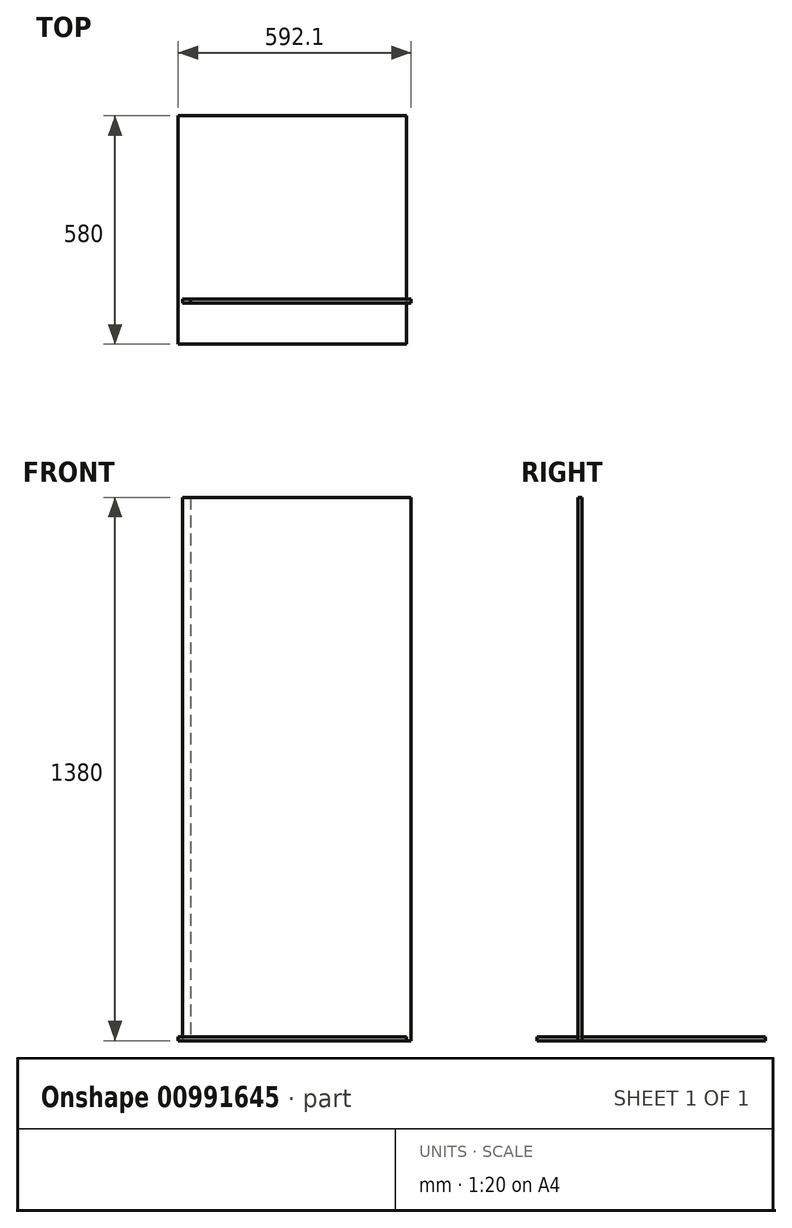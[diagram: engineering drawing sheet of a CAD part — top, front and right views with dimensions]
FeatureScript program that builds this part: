
annotation { "Feature Type Name" : "Feature", "Feature Type Description" : "" }
export const myFeature = defineFeature(function(context is Context, id is Id, definition is map)
    precondition{}
    {
        {
            var Q0;
            Q0=qCreatedBy(makeId("Top.planeOp"),FACE);
            var sketch = newSketch(context, id + "F0", { "sketchPlane" : qUnion([Q0])});
            skLineSegment(sketch, "E0.bottom", {"start": v(-278.4, -47.98) * mm, "end": v(301.6, -47.98) * mm});
            skLineSegment(sketch, "E0.top", {"start": v(-278.4, -57.98) * mm, "end": v(301.6, -57.98) * mm});
            skLineSegment(sketch, "E0.left", {"start": v(-278.4, -47.98) * mm, "end": v(-278.4, -57.98) * mm});
            skLineSegment(sketch, "E0.right", {"start": v(301.6, -47.98) * mm, "end": v(301.6, -57.98) * mm});
            skSolve(sketch);
        }
        {
            var Q0;
            Q0=qCreatedBy(makeId("Top.planeOp"),FACE);
            var sketch = newSketch(context, id + "F1", { "sketchPlane" : qUnion([Q0])});
            skLineSegment(sketch, "E1.bottom", {"start": v(-257.6, -47.91) * mm, "end": v(302.4, -47.91) * mm});
            skLineSegment(sketch, "E1.top", {"start": v(-257.6, -57.91) * mm, "end": v(302.4, -57.91) * mm});
            skLineSegment(sketch, "E1.left", {"start": v(-257.6, -47.91) * mm, "end": v(-257.6, -57.91) * mm});
            skLineSegment(sketch, "E1.right", {"start": v(302.4, -47.91) * mm, "end": v(302.4, -57.91) * mm});
            skSolve(sketch);
        }
        {
            var Q0;
            Q0 = qSketchRegion(id + "F0", true);
            extrude(context, id + "F2", {"entities" : qUnion([Q0]), "depth" : 1380 * mm, "offsetDistance" : 25 * mm});
        }
        {
            var Q0;
            Q0 = qSketchRegion(id + "F1", true);
            extrude(context, id + "F3", {"entities" : qUnion([Q0]), "depth" : 1380 * mm, "offsetDistance" : 25 * mm});
        }
        {
            var Q0;
            Q0=qCreatedBy(makeId("Top.planeOp"),FACE);
            var sketch = newSketch(context, id + "F4", { "sketchPlane" : qUnion([Q0])});
            skLineSegment(sketch, "E2.bottom", {"start": v(-289.7, 417.88) * mm, "end": v(290.3, 417.88) * mm});
            skLineSegment(sketch, "E2.top", {"start": v(-289.7, -162.12) * mm, "end": v(290.3, -162.12) * mm});
            skLineSegment(sketch, "E2.left", {"start": v(-289.7, 417.88) * mm, "end": v(-289.7, -162.12) * mm});
            skLineSegment(sketch, "E2.right", {"start": v(290.3, 417.88) * mm, "end": v(290.3, -162.12) * mm});
            skSolve(sketch);
        }
        {
            var Q0;
            Q0 = qSketchRegion(id + "F4", true);
            extrude(context, id + "F5", {"entities" : qUnion([Q0]), "depth" : 10 * mm, "offsetDistance" : 25 * mm});
        }
    });
